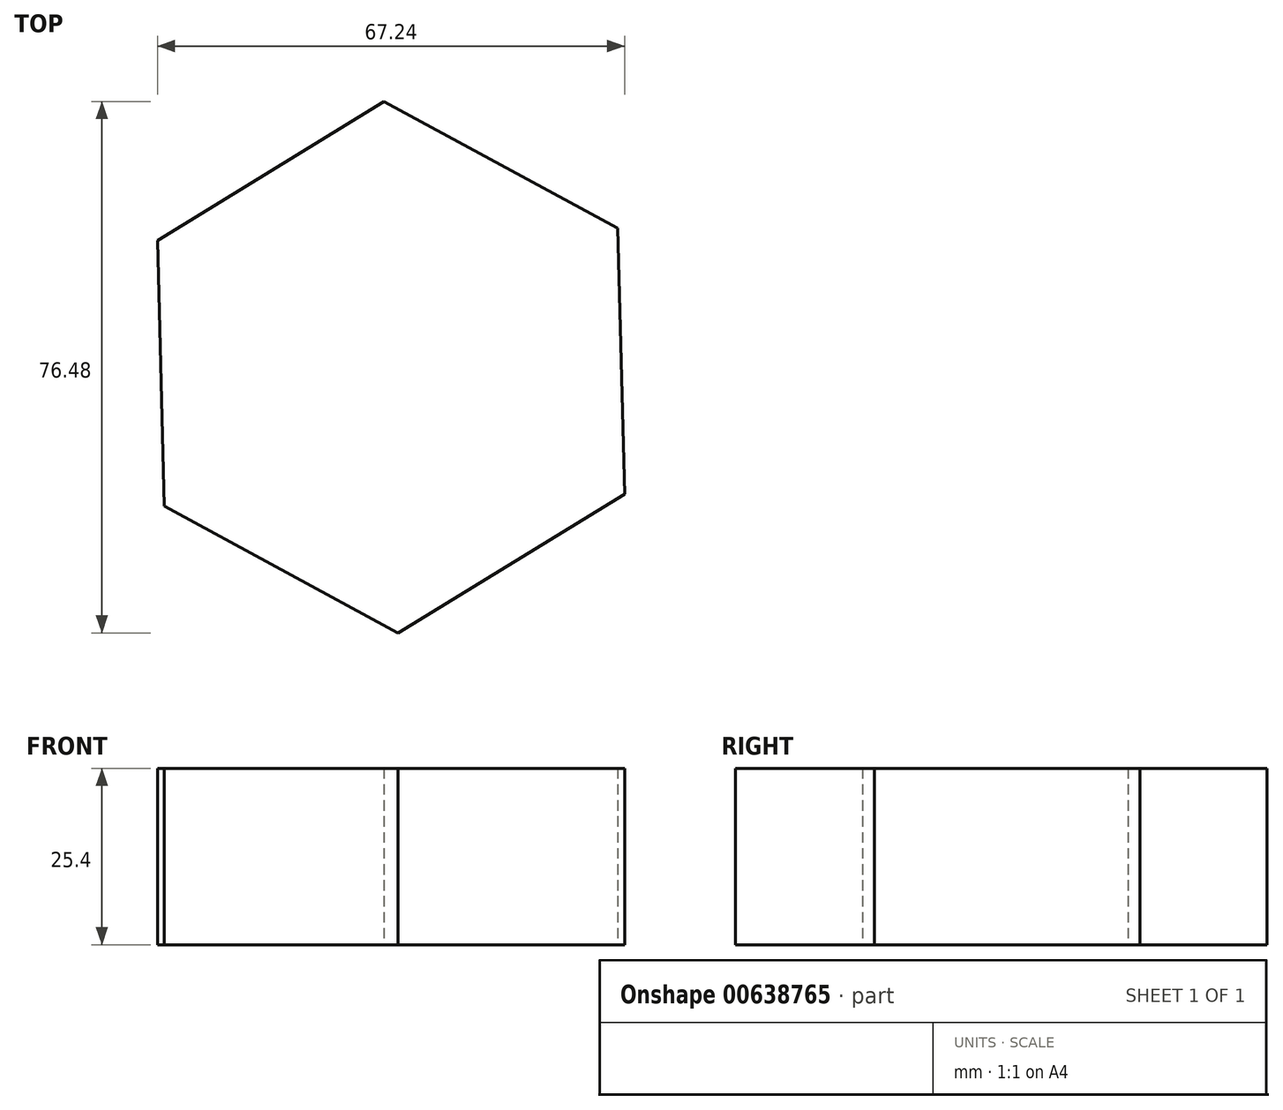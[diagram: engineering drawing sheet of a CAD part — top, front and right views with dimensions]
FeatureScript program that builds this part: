
annotation { "Feature Type Name" : "Feature", "Feature Type Description" : "" }
export const myFeature = defineFeature(function(context is Context, id is Id, definition is map)
    precondition{}
    {
        {
            var Q0;
            Q0=qCreatedBy(makeId("Top.planeOp"),FACE);
            var sketch = newSketch(context, id + "F0", { "sketchPlane" : qUnion([Q0])});
            skCircle(sketch, "E0.cCircle", {"center": v(0, 0) * mm, "radius": 33.13 * mm, "construction": true});
            skLineSegment(sketch, "E0.0", {"start": v(-33.62, 18.25) * mm, "end": v(-1, 38.24) * mm});
            skLineSegment(sketch, "E0.1", {"start": v(-1, 38.24) * mm, "end": v(32.62, 20) * mm});
            skLineSegment(sketch, "E0.2", {"start": v(32.62, 20) * mm, "end": v(33.62, -18.25) * mm});
            skLineSegment(sketch, "E0.3", {"start": v(33.62, -18.25) * mm, "end": v(1, -38.24) * mm});
            skLineSegment(sketch, "E0.4", {"start": v(1, -38.24) * mm, "end": v(-32.62, -20) * mm});
            skLineSegment(sketch, "E0.5", {"start": v(-32.62, -20) * mm, "end": v(-33.62, 18.25) * mm});
            skPoint(sketch, "E0.0.midPoint", {"position": v(-17.31, 28.25) * mm});
            skSolve(sketch);
        }
        {
            var Q0;
            Q0=makeQuery(id+"F0.imprint","IMPRINT",FACE,{"disambiguationData":[TD([[makeQuery(id+"F0.imprint","IMPRINT",EDGE,{"derivedFrom":sQuery(id+"F0.wireOp",EDGE,"E0.0")}),-1.0]])]});
            extrude(context, id + "F1", {"entities" : qUnion([Q0]), "depth" : 25.4 * mm, "offsetDistance" : 25.4 * mm});
        }
        {
            var Q0;
            Q0=qCreatedBy(makeId("Top.planeOp"),FACE);
            var sketch = newSketch(context, id + "F2", { "sketchPlane" : qUnion([Q0])});
            skCircle(sketch, "E1.cCircle", {"center": v(-21.82, 40.05) * mm, "radius": 7.07 * mm, "construction": true});
            skLineSegment(sketch, "E1.0", {"start": v(-29.76, 41.93) * mm, "end": v(-24.16, 47.86) * mm});
            skLineSegment(sketch, "E1.1", {"start": v(-24.16, 47.86) * mm, "end": v(-16.22, 45.99) * mm});
            skLineSegment(sketch, "E1.2", {"start": v(-16.22, 45.99) * mm, "end": v(-13.88, 38.17) * mm});
            skLineSegment(sketch, "E1.3", {"start": v(-13.88, 38.17) * mm, "end": v(-19.47, 32.24) * mm});
            skLineSegment(sketch, "E1.4", {"start": v(-19.47, 32.24) * mm, "end": v(-27.41, 34.11) * mm});
            skLineSegment(sketch, "E1.5", {"start": v(-27.41, 34.11) * mm, "end": v(-29.76, 41.93) * mm});
            skPoint(sketch, "E1.0.midPoint", {"position": v(-26.96, 44.9) * mm});
            skSolve(sketch);
        }
        {
            var Q0;
            Q0=sQuery(id+"F2.wireOp",EDGE,"E1.1");
            var Q1;
            Q1=sQuery(id+"F2.wireOp",EDGE,"E1.2");
            extrude(context, id + "F3", {"bodyType" : ToolBodyType.SURFACE, "surfaceEntities" : qUnion([Q0, Q1]), "depth" : 25.4 * mm, "offsetDistance" : 25.4 * mm});
        }
    });
